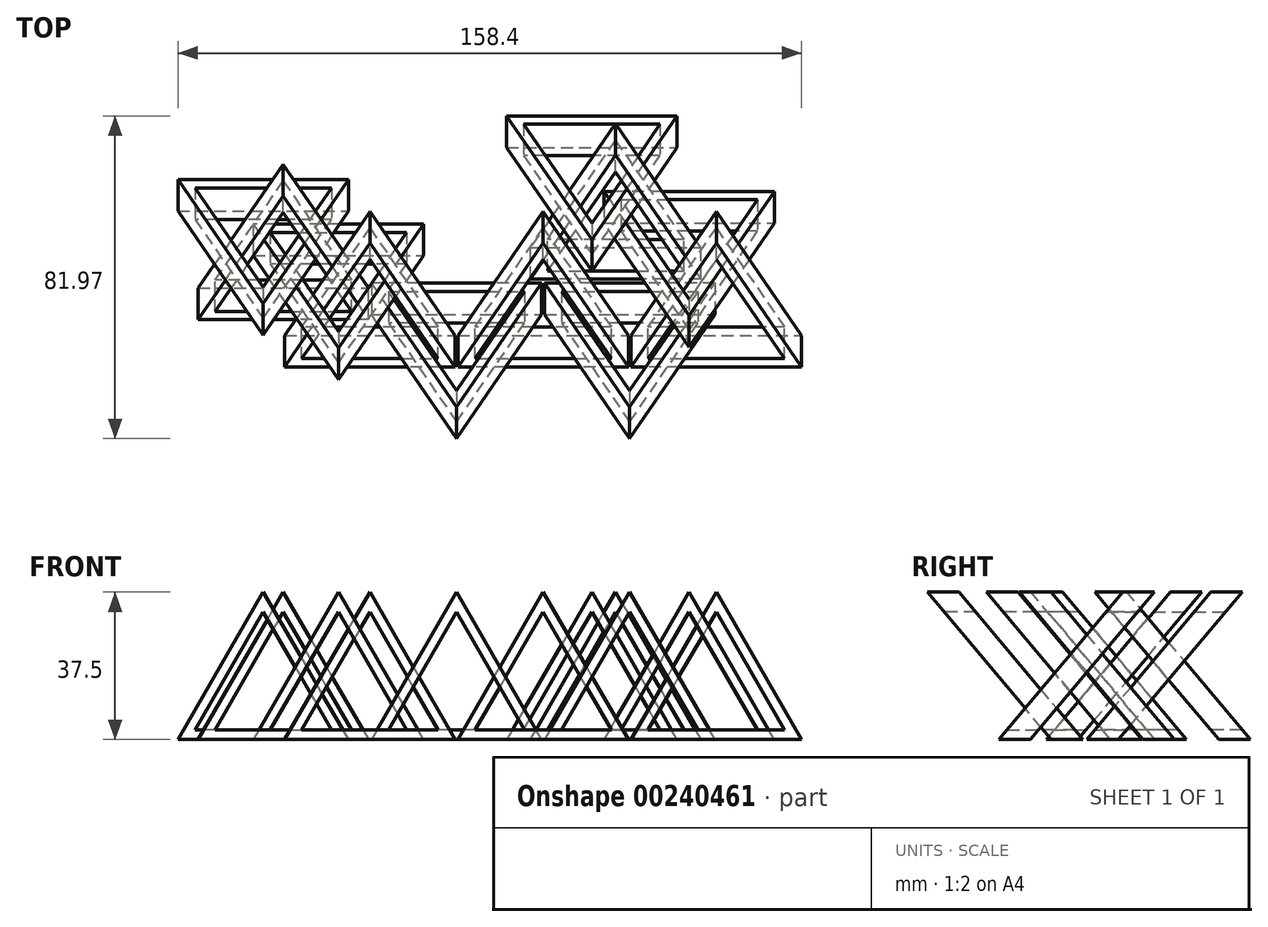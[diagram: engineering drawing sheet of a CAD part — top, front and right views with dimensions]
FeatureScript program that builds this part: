
annotation { "Feature Type Name" : "Feature", "Feature Type Description" : "" }
export const myFeature = defineFeature(function(context is Context, id is Id, definition is map)
    precondition{}
    {
        {
            var Q0;
            Q0=qCreatedBy(makeId("Front.planeOp"),FACE);
            var sketch = newSketch(context, id + "F0", { "sketchPlane" : qUnion([Q0])});
            skCircle(sketch, "E0.cCircle", {"center": v(0, 0) * mm, "radius": 12.5 * mm, "construction": true});
            skLineSegment(sketch, "E0.0", {"start": v(21.65, -12.5) * mm, "end": v(-21.65, -12.5) * mm});
            skLineSegment(sketch, "E0.1", {"start": v(-21.65, -12.5) * mm, "end": v(0, 25) * mm});
            skLineSegment(sketch, "E0.2", {"start": v(0, 25) * mm, "end": v(21.65, -12.5) * mm});
            skPoint(sketch, "E0.0.midPoint", {"position": v(0, -12.5) * mm});
            skSolve(sketch);
        }
        {
            var Q0;
            Q0=makeQuery(id+"F0.imprint","IMPRINT",FACE,{"disambiguationData":[TD([[makeQuery(id+"F0.imprint","IMPRINT",EDGE,{"derivedFrom":sQuery(id+"F0.wireOp",EDGE,"E0.0")}),-1.0]])]});
            extrude(context, id + "F1", {"entities" : qUnion([Q0]), "depth" : 50 * mm});
        }
        {
            var Q0;
            Q0=makeQuery(id+"F1.opExtrude","CAP_FACE",FACE,{"disambiguationData":[OSD([sQuery(id+"F0.wireOp",EDGE,"E0.0"),sQuery(id+"F0.wireOp",EDGE,"E0.1"),sQuery(id+"F0.wireOp",EDGE,"E0.2")])],"isStart":true});
            var sketch = newSketch(context, id + "F2", { "sketchPlane" : qUnion([Q0])});
            skCircle(sketch, "E1.cCircle", {"center": v(0, 0) * mm, "radius": 10 * mm, "construction": true});
            skLineSegment(sketch, "E1.0", {"start": v(17.32, -10) * mm, "end": v(-17.32, -10) * mm});
            skLineSegment(sketch, "E1.1", {"start": v(-17.32, -10) * mm, "end": v(0, 20) * mm});
            skLineSegment(sketch, "E1.2", {"start": v(0, 20) * mm, "end": v(17.32, -10) * mm});
            skPoint(sketch, "E1.0.midPoint", {"position": v(0, -10) * mm});
            skSolve(sketch);
        }
        {
            var Q0;
            Q0=makeQuery(id+"F2.imprint","IMPRINT",FACE,{"disambiguationData":[TD([[makeQuery(id+"F2.imprint","IMPRINT",EDGE,{"derivedFrom":sQuery(id+"F2.wireOp",EDGE,"E1.0")}),-1.0]])]});
            extrude(context, id + "F3", {"entities" : qUnion([Q0]), "operationType" : NewBodyOperationType.REMOVE, "endBound" : BoundingType.THROUGH_ALL, "oppositeDirection" : true, "depth" : 25 * mm});
        }
        {
            var Q0;
            Q0=qCreatedBy(makeId("Right.planeOp"),FACE);
            var sketch = newSketch(context, id + "F4", { "sketchPlane" : qUnion([Q0])});
            skLineSegment(sketch, "E2", {"start": v(0, 29.38) * mm, "end": v(-38.07, -15.99) * mm});
            skLineSegment(sketch, "E3", {"start": v(-38.07, -15.99) * mm, "end": v(-46.07, -15.99) * mm});
            skLineSegment(sketch, "E4", {"start": v(-46.07, -15.99) * mm, "end": v(-6.52, 31.14) * mm});
            skLineSegment(sketch, "E5", {"start": v(-6.52, 31.14) * mm, "end": v(0, 29.38) * mm});
            skSolve(sketch);
        }
        {
            var Q0;
            Q0=makeQuery(id+"F4.imprint","IMPRINT",FACE,{"disambiguationData":[TD([[makeQuery(id+"F4.imprint","IMPRINT",EDGE,{"derivedFrom":sQuery(id+"F4.wireOp",EDGE,"E2")}),-1.0]])]});
            extrude(context, id + "F5", {"entities" : qUnion([Q0]), "operationType" : NewBodyOperationType.INTERSECT, "depth" : 25 * mm, "hasSecondDirection" : true, "secondDirectionOppositeDirection" : true, "secondDirectionDepth" : 25 * mm});
        }
        {
            var Q0;
            Q0=makeQuery(id+"F1.opExtrude","SWEPT_BODY",BODY,{"disambiguationData":[OSD([sQuery(id+"F0.wireOp",EDGE,"E0.0"),sQuery(id+"F0.wireOp",EDGE,"E0.1"),sQuery(id+"F0.wireOp",EDGE,"E0.2")])]});
            var Q1;
            Q1=qCreatedBy(makeId("Front.planeOp"),FACE);
            mirror(context, id + "F6", {"entities" : qUnion([Q0]), "mirrorPlane" : qUnion([Q1])});
        }
        {
            var Q0;
            Q0=makeQuery(id+"F6.opPattern","COPY",BODY,{"derivedFrom":makeQuery(id+"F1.opExtrude","SWEPT_BODY",BODY,{"disambiguationData":[OSD([sQuery(id+"F0.wireOp",EDGE,"E0.0"),sQuery(id+"F0.wireOp",EDGE,"E0.1"),sQuery(id+"F0.wireOp",EDGE,"E0.2")])]}),"instanceName":"1"});
            transform(context, id + "F7", {"entities" : qUnion([Q0]), "transformType" : TransformType.TRANSLATION_3D, "dx" : -22 * mm, "dy" : -65 * mm, "dz" : 0 * mm, "makeCopy" : true});
        }
        {
            var Q0;
            Q0=makeQuery(id+"F6.opPattern","COPY",BODY,{"derivedFrom":makeQuery(id+"F1.opExtrude","SWEPT_BODY",BODY,{"disambiguationData":[OSD([sQuery(id+"F0.wireOp",EDGE,"E0.0"),sQuery(id+"F0.wireOp",EDGE,"E0.1"),sQuery(id+"F0.wireOp",EDGE,"E0.2")])]}),"instanceName":"1"});
            transform(context, id + "F8", {"entities" : qUnion([Q0]), "transformType" : TransformType.TRANSLATION_3D, "dx" : 22 * mm, "dy" : -65 * mm, "dz" : 0 * mm, "makeCopy" : false});
        }
        {
            var Q0;
            Q0=makeQuery(id+"F1.opExtrude","SWEPT_BODY",BODY,{"disambiguationData":[OSD([sQuery(id+"F0.wireOp",EDGE,"E0.0"),sQuery(id+"F0.wireOp",EDGE,"E0.1"),sQuery(id+"F0.wireOp",EDGE,"E0.2")])]});
            transform(context, id + "F9", {"entities" : qUnion([Q0]), "transformType" : TransformType.TRANSLATION_3D, "dx" : -44 * mm, "dy" : 0 * mm, "dz" : 0 * mm, "makeCopy" : true});
        }
        {
            var Q0;
            Q0=makeQuery(id+"F1.opExtrude","SWEPT_BODY",BODY,{"disambiguationData":[OSD([sQuery(id+"F0.wireOp",EDGE,"E0.0"),sQuery(id+"F0.wireOp",EDGE,"E0.1"),sQuery(id+"F0.wireOp",EDGE,"E0.2")])]});
            transform(context, id + "F10", {"entities" : qUnion([Q0]), "transformType" : TransformType.TRANSLATION_3D, "dx" : 44 * mm, "dy" : 0 * mm, "dz" : 0 * mm, "makeCopy" : true});
        }
        {
            var Q0;
            Q0=makeQuery(id+"F7.opPattern","COPY",BODY,{"derivedFrom":makeQuery(id+"F6.opPattern","COPY",BODY,{"derivedFrom":makeQuery(id+"F1.opExtrude","SWEPT_BODY",BODY,{"disambiguationData":[OSD([sQuery(id+"F0.wireOp",EDGE,"E0.0"),sQuery(id+"F0.wireOp",EDGE,"E0.1"),sQuery(id+"F0.wireOp",EDGE,"E0.2")])]}),"instanceName":"1"}),"instanceName":"1"});
            transform(context, id + "F11", {"entities" : qUnion([Q0]), "transformType" : TransformType.TRANSLATION_3D, "dx" : -30 * mm, "dy" : 15 * mm, "dz" : 0 * mm, "makeCopy" : true});
        }
        {
            var Q0;
            Q0=makeQuery(id+"F9.opPattern","COPY",BODY,{"derivedFrom":makeQuery(id+"F1.opExtrude","SWEPT_BODY",BODY,{"disambiguationData":[OSD([sQuery(id+"F0.wireOp",EDGE,"E0.0"),sQuery(id+"F0.wireOp",EDGE,"E0.1"),sQuery(id+"F0.wireOp",EDGE,"E0.2")])]}),"instanceName":"1"});
            transform(context, id + "F12", {"entities" : qUnion([Q0]), "transformType" : TransformType.TRANSLATION_3D, "dx" : -22 * mm, "dy" : 12 * mm, "dz" : 0 * mm, "makeCopy" : true});
        }
        {
            var Q0;
            Q0=makeQuery(id+"F11.opPattern","COPY",BODY,{"derivedFrom":makeQuery(id+"F7.opPattern","COPY",BODY,{"derivedFrom":makeQuery(id+"F6.opPattern","COPY",BODY,{"derivedFrom":makeQuery(id+"F1.opExtrude","SWEPT_BODY",BODY,{"disambiguationData":[OSD([sQuery(id+"F0.wireOp",EDGE,"E0.0"),sQuery(id+"F0.wireOp",EDGE,"E0.1"),sQuery(id+"F0.wireOp",EDGE,"E0.2")])]}),"instanceName":"1"}),"instanceName":"1"}),"instanceName":"1"});
            transform(context, id + "F13", {"entities" : qUnion([Q0]), "transformType" : TransformType.TRANSLATION_3D, "dx" : -19.1 * mm, "dy" : 11.3 * mm, "dz" : 0 * mm, "makeCopy" : true});
        }
        {
            var Q0;
            Q0=makeQuery(id+"F6.opPattern","COPY",BODY,{"derivedFrom":makeQuery(id+"F1.opExtrude","SWEPT_BODY",BODY,{"disambiguationData":[OSD([sQuery(id+"F0.wireOp",EDGE,"E0.0"),sQuery(id+"F0.wireOp",EDGE,"E0.1"),sQuery(id+"F0.wireOp",EDGE,"E0.2")])]}),"instanceName":"1"});
            transform(context, id + "F14", {"entities" : qUnion([Q0]), "transformType" : TransformType.TRANSLATION_3D, "dx" : 15.1 * mm, "dy" : 23.3 * mm, "dz" : 0 * mm, "makeCopy" : true});
        }
        {
            var Q0;
            Q0=makeQuery(id+"F1.opExtrude","SWEPT_BODY",BODY,{"disambiguationData":[OSD([sQuery(id+"F0.wireOp",EDGE,"E0.0"),sQuery(id+"F0.wireOp",EDGE,"E0.1"),sQuery(id+"F0.wireOp",EDGE,"E0.2")])]});
            transform(context, id + "F15", {"entities" : qUnion([Q0]), "transformType" : TransformType.TRANSLATION_3D, "dx" : 18.4 * mm, "dy" : 22.3 * mm, "dz" : 0 * mm, "makeCopy" : true});
        }
        {
            var Q0;
            Q0=makeQuery(id+"F14.opPattern","COPY",BODY,{"derivedFrom":makeQuery(id+"F6.opPattern","COPY",BODY,{"derivedFrom":makeQuery(id+"F1.opExtrude","SWEPT_BODY",BODY,{"disambiguationData":[OSD([sQuery(id+"F0.wireOp",EDGE,"E0.0"),sQuery(id+"F0.wireOp",EDGE,"E0.1"),sQuery(id+"F0.wireOp",EDGE,"E0.2")])]}),"instanceName":"1"}),"instanceName":"1"});
            transform(context, id + "F16", {"entities" : qUnion([Q0]), "transformType" : TransformType.TRANSLATION_3D, "dx" : -24.7 * mm, "dy" : 19.2 * mm, "dz" : 0 * mm, "makeCopy" : true});
        }
    });
